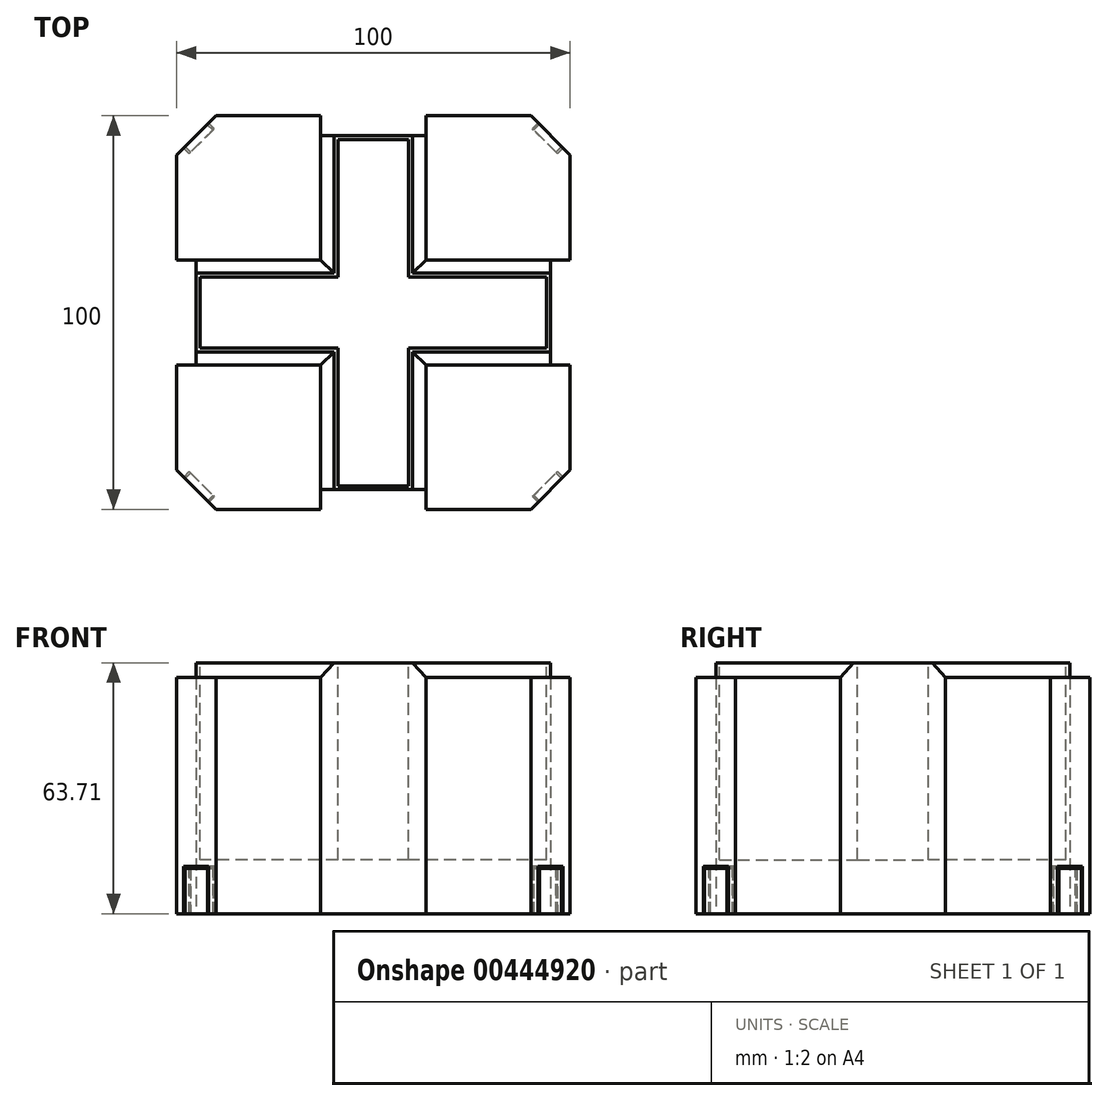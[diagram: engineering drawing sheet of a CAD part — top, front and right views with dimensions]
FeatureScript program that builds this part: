
annotation { "Feature Type Name" : "Feature", "Feature Type Description" : "" }
export const myFeature = defineFeature(function(context is Context, id is Id, definition is map)
    precondition{}
    {
        {
            var Q0;
            Q0=qCreatedBy(makeId("Front.planeOp"),FACE);
            var sketch = newSketch(context, id + "F0", { "sketchPlane" : qUnion([Q0])});
            skLineSegment(sketch, "E0.bottom", {"start": v(50, -30) * mm, "end": v(-50, -30) * mm});
            skLineSegment(sketch, "E0.left", {"start": v(50, -30) * mm, "end": v(50, 30) * mm});
            skLineSegment(sketch, "E0.right", {"start": v(-50, -30) * mm, "end": v(-50, 30) * mm});
            skPoint(sketch, "E0.middle", {"position": v(0, 0) * mm});
            skPoint(sketch, "E1.endSnap0", {"position": v(0, -30) * mm});
            skLineSegment(sketch, "E2", {"start": v(50, 30) * mm, "end": v(13.35, 30) * mm});
            skLineSegment(sketch, "E3", {"start": v(13.35, 30) * mm, "end": v(10, 33.7) * mm});
            skLineSegment(sketch, "E4", {"start": v(10, 33.7) * mm, "end": v(0, 33.7) * mm});
            skLineSegment(sketch, "E5.MirrorCS", {"start": v(-10, 33.7) * mm, "end": v(0, 33.7) * mm});
            skLineSegment(sketch, "E6.MirrorCS", {"start": v(-13.35, 30) * mm, "end": v(-10, 33.7) * mm});
            skLineSegment(sketch, "E7.MirrorCS", {"start": v(-50, 30) * mm, "end": v(-13.35, 30) * mm});
            skSolve(sketch);
        }
        {
            var Q0;
            Q0 = qSketchRegion(id + "F0", true);
            extrude(context, id + "F1", {"entities" : qUnion([Q0]), "endBound" : BoundingType.SYMMETRIC, "depth" : 100 * mm});
        }
        {
            var Q0;
            Q0=qCreatedBy(makeId("Right.planeOp"),FACE);
            var sketch = newSketch(context, id + "F2", { "sketchPlane" : qUnion([Q0])});
            skLineSegment(sketch, "E8", {"start": v(0, 33.7) * mm, "end": v(-10, 33.7) * mm});
            skLineSegment(sketch, "E9", {"start": v(-10, 33.7) * mm, "end": v(-13.35, 30) * mm});
            skLineSegment(sketch, "E10", {"start": v(-13.35, 30) * mm, "end": v(-50, 30) * mm});
            skLineSegment(sketch, "E11", {"start": v(-50, 30) * mm, "end": v(-50, -30) * mm});
            skLineSegment(sketch, "E12", {"start": v(-50, -30) * mm, "end": v(0, -30) * mm});
            skLineSegment(sketch, "E13.MirrorCS", {"start": v(0, 33.7) * mm, "end": v(10, 33.7) * mm});
            skLineSegment(sketch, "E14.MirrorCS", {"start": v(13.35, 30) * mm, "end": v(50, 30) * mm});
            skLineSegment(sketch, "E15.MirrorCS", {"start": v(50, 30) * mm, "end": v(50, -30) * mm});
            skLineSegment(sketch, "E16.MirrorCS", {"start": v(50, -30) * mm, "end": v(0, -30) * mm});
            skLineSegment(sketch, "E17.MirrorCS", {"start": v(10, 33.7) * mm, "end": v(13.35, 30) * mm});
            skSolve(sketch);
        }
        {
            var Q0;
            Q0 = qSketchRegion(id + "F2", true);
            extrude(context, id + "F3", {"entities" : qUnion([Q0]), "operationType" : NewBodyOperationType.ADD, "endBound" : BoundingType.SYMMETRIC, "depth" : 100 * mm});
        }
        {
            var Q0;
            Q0=makeQuery(id+"F3.boolean.opBoolean","MERGE",FACE,{"derivedFrom":[makeQuery(id+"F1.opExtrude","SWEPT_FACE",FACE,{"disambiguationData":[OSD([sQuery(id+"F0.wireOp",EDGE,"E0.right")])]}),makeQuery(id+"F3.opExtrude","CAP_FACE",FACE,{"disambiguationData":[OSD([sQuery(id+"F2.wireOp",EDGE,"E8"),sQuery(id+"F2.wireOp",EDGE,"E9"),sQuery(id+"F2.wireOp",EDGE,"E10"),sQuery(id+"F2.wireOp",EDGE,"E11"),sQuery(id+"F2.wireOp",EDGE,"E12"),sQuery(id+"F2.wireOp",EDGE,"E13.MirrorCS"),sQuery(id+"F2.wireOp",EDGE,"E14.MirrorCS"),sQuery(id+"F2.wireOp",EDGE,"E15.MirrorCS"),sQuery(id+"F2.wireOp",EDGE,"E16.MirrorCS"),sQuery(id+"F2.wireOp",EDGE,"E17.MirrorCS")])],"isStart":true})]});
            var sketch = newSketch(context, id + "F4", { "sketchPlane" : qUnion([Q0])});
            skLineSegment(sketch, "E18", {"start": v(-10, 33.7) * mm, "end": v(-13.35, 30) * mm});
            skLineSegment(sketch, "E19", {"start": v(-13.35, 30) * mm, "end": v(-13.35, -30) * mm});
            skLineSegment(sketch, "E20", {"start": v(-10, 33.7) * mm, "end": v(10, 33.7) * mm});
            skLineSegment(sketch, "E21", {"start": v(10, 33.7) * mm, "end": v(13.35, 30) * mm});
            skLineSegment(sketch, "E22", {"start": v(13.35, 30) * mm, "end": v(13.35, -30) * mm});
            skLineSegment(sketch, "E23", {"start": v(13.35, -30) * mm, "end": v(-13.35, -30) * mm});
            skSolve(sketch);
        }
        {
            var Q0;
            Q0 = qSketchRegion(id + "F4", true);
            extrude(context, id + "F5", {"entities" : qUnion([Q0]), "operationType" : NewBodyOperationType.REMOVE, "oppositeDirection" : true, "depth" : 5 * mm});
        }
        {
            var Q0;
            Q0=makeQuery(id+"F1.opExtrude","CAP_FACE",FACE,{"disambiguationData":[OSD([sQuery(id+"F0.wireOp",EDGE,"E0.bottom"),sQuery(id+"F0.wireOp",EDGE,"E0.left"),sQuery(id+"F0.wireOp",EDGE,"E0.right"),sQuery(id+"F0.wireOp",EDGE,"E2"),sQuery(id+"F0.wireOp",EDGE,"E3"),sQuery(id+"F0.wireOp",EDGE,"E4"),sQuery(id+"F0.wireOp",EDGE,"E5.MirrorCS"),sQuery(id+"F0.wireOp",EDGE,"E6.MirrorCS"),sQuery(id+"F0.wireOp",EDGE,"E7.MirrorCS")])],"isStart":false});
            var sketch = newSketch(context, id + "F6", { "sketchPlane" : qUnion([Q0])});
            skLineSegment(sketch, "E24", {"start": v(-13.35, 30) * mm, "end": v(-10, 33.7) * mm});
            skLineSegment(sketch, "E25", {"start": v(-10, 33.7) * mm, "end": v(10, 33.7) * mm});
            skLineSegment(sketch, "E26", {"start": v(10, 33.7) * mm, "end": v(13.35, 30) * mm});
            skLineSegment(sketch, "E27", {"start": v(13.35, 30) * mm, "end": v(13.35, -30) * mm});
            skLineSegment(sketch, "E28", {"start": v(13.35, -30) * mm, "end": v(-13.35, -30) * mm});
            skLineSegment(sketch, "E29", {"start": v(-13.35, -30) * mm, "end": v(-13.35, 30) * mm});
            skSolve(sketch);
        }
        {
            var Q0;
            Q0 = qSketchRegion(id + "F6", true);
            extrude(context, id + "F7", {"entities" : qUnion([Q0]), "operationType" : NewBodyOperationType.REMOVE, "oppositeDirection" : true, "depth" : 5 * mm});
        }
        {
            var Q0;
            Q0=makeQuery(id+"F3.boolean.opBoolean","MERGE",FACE,{"derivedFrom":[makeQuery(id+"F1.opExtrude","SWEPT_FACE",FACE,{"disambiguationData":[OSD([sQuery(id+"F0.wireOp",EDGE,"E0.left")])]}),makeQuery(id+"F3.opExtrude","CAP_FACE",FACE,{"disambiguationData":[OSD([sQuery(id+"F2.wireOp",EDGE,"E8"),sQuery(id+"F2.wireOp",EDGE,"E9"),sQuery(id+"F2.wireOp",EDGE,"E10"),sQuery(id+"F2.wireOp",EDGE,"E11"),sQuery(id+"F2.wireOp",EDGE,"E12"),sQuery(id+"F2.wireOp",EDGE,"E13.MirrorCS"),sQuery(id+"F2.wireOp",EDGE,"E14.MirrorCS"),sQuery(id+"F2.wireOp",EDGE,"E15.MirrorCS"),sQuery(id+"F2.wireOp",EDGE,"E16.MirrorCS"),sQuery(id+"F2.wireOp",EDGE,"E17.MirrorCS")])],"isStart":false})]});
            var sketch = newSketch(context, id + "F8", { "sketchPlane" : qUnion([Q0])});
            skLineSegment(sketch, "E30", {"start": v(-13.35, 30) * mm, "end": v(-10, 33.7) * mm});
            skLineSegment(sketch, "E31", {"start": v(-10, 33.7) * mm, "end": v(10, 33.7) * mm});
            skLineSegment(sketch, "E32", {"start": v(10, 33.7) * mm, "end": v(13.35, 30) * mm});
            skLineSegment(sketch, "E33", {"start": v(13.35, 30) * mm, "end": v(13.35, -30) * mm});
            skLineSegment(sketch, "E34", {"start": v(13.35, -30) * mm, "end": v(-13.35, -30) * mm});
            skLineSegment(sketch, "E35", {"start": v(-13.35, -30) * mm, "end": v(-13.35, 30) * mm});
            skSolve(sketch);
        }
        {
            var Q0;
            Q0 = qSketchRegion(id + "F8", true);
            extrude(context, id + "F9", {"entities" : qUnion([Q0]), "operationType" : NewBodyOperationType.REMOVE, "oppositeDirection" : true, "depth" : 5 * mm});
        }
        {
            var Q0;
            Q0=makeQuery(id+"F1.opExtrude","CAP_FACE",FACE,{"disambiguationData":[OSD([sQuery(id+"F0.wireOp",EDGE,"E0.bottom"),sQuery(id+"F0.wireOp",EDGE,"E0.left"),sQuery(id+"F0.wireOp",EDGE,"E0.right"),sQuery(id+"F0.wireOp",EDGE,"E2"),sQuery(id+"F0.wireOp",EDGE,"E3"),sQuery(id+"F0.wireOp",EDGE,"E4"),sQuery(id+"F0.wireOp",EDGE,"E5.MirrorCS"),sQuery(id+"F0.wireOp",EDGE,"E6.MirrorCS"),sQuery(id+"F0.wireOp",EDGE,"E7.MirrorCS")])],"isStart":true});
            var sketch = newSketch(context, id + "F10", { "sketchPlane" : qUnion([Q0])});
            skLineSegment(sketch, "E36", {"start": v(-13.35, 30) * mm, "end": v(-10, 33.7) * mm});
            skLineSegment(sketch, "E37", {"start": v(-10, 33.7) * mm, "end": v(10, 33.7) * mm});
            skLineSegment(sketch, "E38", {"start": v(10, 33.7) * mm, "end": v(13.35, 30) * mm});
            skLineSegment(sketch, "E39", {"start": v(13.35, 30) * mm, "end": v(13.35, -30) * mm});
            skLineSegment(sketch, "E40", {"start": v(13.35, -30) * mm, "end": v(-13.35, -30) * mm});
            skLineSegment(sketch, "E41", {"start": v(-13.35, -30) * mm, "end": v(-13.35, 30) * mm});
            skSolve(sketch);
        }
        {
            var Q0;
            Q0 = qSketchRegion(id + "F10", true);
            extrude(context, id + "F11", {"entities" : qUnion([Q0]), "operationType" : NewBodyOperationType.REMOVE, "oppositeDirection" : true, "depth" : 5 * mm});
        }
        {
            var Q0;
            Q0=makeQuery(id+"F1.opExtrude","CAP_EDGE",EDGE,{"disambiguationData":[OSD([sQuery(id+"F0.wireOp",EDGE,"E0.left")])],"isStart":false});
            var Q1;
            Q1=makeQuery(id+"F1.opExtrude","CAP_EDGE",EDGE,{"disambiguationData":[OSD([sQuery(id+"F0.wireOp",EDGE,"E0.left")])],"isStart":true});
            var Q2;
            Q2=makeQuery(id+"F1.opExtrude","CAP_EDGE",EDGE,{"disambiguationData":[OSD([sQuery(id+"F0.wireOp",EDGE,"E0.right")])],"isStart":true});
            var Q3;
            Q3=makeQuery(id+"F1.opExtrude","CAP_EDGE",EDGE,{"disambiguationData":[OSD([sQuery(id+"F0.wireOp",EDGE,"E0.right")])],"isStart":false});
            chamfer(context, id + "F12", {"entities" : qUnion([Q0, Q1, Q2, Q3]), "width" : 10 * mm, "tangentPropagation" : true});
        }
        {
            var Q0;
            {var subQ0=sQuery(id+"F0.wireOp",EDGE,"E0.right");Q0=makeQuery(id+"F12.opChamfer","BLEND_FACE",FACE,{"disambiguationData":[OSD([subQ0]),TDD([makeQuery(id+"F1.opExtrude","CAP_EDGE",EDGE,{"disambiguationData":[OSD([subQ0])],"isStart":true})])]});}
            var sketch = newSketch(context, id + "F13", { "sketchPlane" : qUnion([Q0])});
            skLineSegment(sketch, "E42", {"start": v(-4.48, -30) * mm, "end": v(-4.48, -18) * mm});
            skLineSegment(sketch, "E43", {"start": v(-4.48, -18) * mm, "end": v(4.52, -18) * mm});
            skLineSegment(sketch, "E44", {"start": v(4.52, -18) * mm, "end": v(4.52, -30) * mm});
            skSolve(sketch);
        }
        {
            var Q0;
            {var subQ0=sQuery(id+"F13.wireOp",EDGE,"E42");Q0=makeQuery(id+"F13.imprint","IMPRINT",FACE,{"disambiguationData":[TD([[makeQuery(id+"F13.imprint","IMPRINT",EDGE,{"derivedFrom":subQ0}),-1.0]])]});}
            extrude(context, id + "F14", {"entities" : qUnion([Q0]), "operationType" : NewBodyOperationType.REMOVE, "oppositeDirection" : true, "depth" : 2 * mm});
        }
        {
            var Q0;
            Q0=makeQuery(id+"F14.boolean.opBoolean","COPY",FACE,{"derivedFrom":makeQuery(id+"F14.opExtrude","CAP_FACE",FACE,{"disambiguationData":[OSD([sQuery(id+"F0.wireOp",EDGE,"E0.bottom"),sQuery(id+"F0.wireOp",EDGE,"E0.right"),sQuery(id+"F13.wireOp",EDGE,"E42"),sQuery(id+"F13.wireOp",EDGE,"E43"),sQuery(id+"F13.wireOp",EDGE,"E44")])],"isStart":false})});
            var sketch = newSketch(context, id + "F15", { "sketchPlane" : qUnion([Q0])});
            skLineSegment(sketch, "E45", {"start": v(-3.98, -30) * mm, "end": v(-3.98, -18.5) * mm});
            skLineSegment(sketch, "E46", {"start": v(-3.98, -18.5) * mm, "end": v(4.02, -18.5) * mm});
            skLineSegment(sketch, "E47", {"start": v(4.02, -18.5) * mm, "end": v(4.02, -30) * mm});
            skLineSegment(sketch, "E48", {"start": v(4.02, -30) * mm, "end": v(-3.98, -30) * mm});
            skSolve(sketch);
        }
        {
            var Q0;
            Q0=makeQuery(id+"F15.imprint","IMPRINT",FACE,{"disambiguationData":[TD([[makeQuery(id+"F15.imprint","IMPRINT",EDGE,{"derivedFrom":sQuery(id+"F15.wireOp",EDGE,"E45")}),-1.0]])]});
            extrude(context, id + "F16", {"entities" : qUnion([Q0]), "operationType" : NewBodyOperationType.ADD, "depth" : 2 * mm});
        }
        {
            var Q0;
            {var subQ0=sQuery(id+"F0.wireOp",EDGE,"E0.right");Q0=makeQuery(id+"F12.opChamfer","BLEND_FACE",FACE,{"disambiguationData":[OSD([subQ0]),TDD([makeQuery(id+"F1.opExtrude","CAP_EDGE",EDGE,{"disambiguationData":[OSD([subQ0])],"isStart":false})])]});}
            var sketch = newSketch(context, id + "F17", { "sketchPlane" : qUnion([Q0])});
            skLineSegment(sketch, "E49", {"start": v(-4.48, -30) * mm, "end": v(-4.48, -18) * mm});
            skLineSegment(sketch, "E50", {"start": v(-4.48, -18) * mm, "end": v(4.52, -18) * mm});
            skLineSegment(sketch, "E51", {"start": v(4.52, -18) * mm, "end": v(4.52, -30) * mm});
            skSolve(sketch);
        }
        {
            var Q0;
            {var subQ0=sQuery(id+"F17.wireOp",EDGE,"E49");Q0=makeQuery(id+"F17.imprint","IMPRINT",FACE,{"disambiguationData":[TD([[makeQuery(id+"F17.imprint","IMPRINT",EDGE,{"derivedFrom":subQ0}),-1.0]])]});}
            extrude(context, id + "F18", {"entities" : qUnion([Q0]), "operationType" : NewBodyOperationType.REMOVE, "oppositeDirection" : true, "depth" : 2 * mm});
        }
        {
            var Q0;
            Q0=makeQuery(id+"F18.boolean.opBoolean","COPY",FACE,{"derivedFrom":makeQuery(id+"F18.opExtrude","CAP_FACE",FACE,{"disambiguationData":[OSD([sQuery(id+"F0.wireOp",EDGE,"E0.bottom"),sQuery(id+"F0.wireOp",EDGE,"E0.right"),sQuery(id+"F17.wireOp",EDGE,"E49"),sQuery(id+"F17.wireOp",EDGE,"E50"),sQuery(id+"F17.wireOp",EDGE,"E51")])],"isStart":false})});
            var sketch = newSketch(context, id + "F19", { "sketchPlane" : qUnion([Q0])});
            skLineSegment(sketch, "E52", {"start": v(-3.98, -30) * mm, "end": v(-3.98, -18.5) * mm});
            skLineSegment(sketch, "E53", {"start": v(-3.98, -18.5) * mm, "end": v(4.02, -18.5) * mm});
            skLineSegment(sketch, "E54", {"start": v(4.02, -18.5) * mm, "end": v(4.02, -30) * mm});
            skLineSegment(sketch, "E55", {"start": v(4.02, -30) * mm, "end": v(-3.98, -30) * mm});
            skSolve(sketch);
        }
        {
            var Q0;
            {var subQ0=sQuery(id+"F0.wireOp",EDGE,"E0.left");Q0=makeQuery(id+"F12.opChamfer","BLEND_FACE",FACE,{"disambiguationData":[OSD([subQ0]),TDD([makeQuery(id+"F1.opExtrude","CAP_EDGE",EDGE,{"disambiguationData":[OSD([subQ0])],"isStart":false})])]});}
            var sketch = newSketch(context, id + "F20", { "sketchPlane" : qUnion([Q0])});
            skLineSegment(sketch, "E56", {"start": v(-4.48, -30) * mm, "end": v(-4.48, -18) * mm});
            skLineSegment(sketch, "E57", {"start": v(-4.48, -18) * mm, "end": v(4.52, -18) * mm});
            skLineSegment(sketch, "E58", {"start": v(4.52, -18) * mm, "end": v(4.52, -30) * mm});
            skLineSegment(sketch, "E59", {"start": v(4.52, -30) * mm, "end": v(-4.48, -30) * mm});
            skSolve(sketch);
        }
        {
            var Q0;
            Q0=makeQuery(id+"F20.imprint","IMPRINT",FACE,{"disambiguationData":[TD([[makeQuery(id+"F20.imprint","IMPRINT",EDGE,{"derivedFrom":sQuery(id+"F20.wireOp",EDGE,"E56")}),-1.0]])]});
            extrude(context, id + "F21", {"entities" : qUnion([Q0]), "operationType" : NewBodyOperationType.REMOVE, "oppositeDirection" : true, "depth" : 2 * mm});
        }
        {
            var Q0;
            Q0=makeQuery(id+"F21.boolean.opBoolean","COPY",FACE,{"derivedFrom":makeQuery(id+"F21.opExtrude","CAP_FACE",FACE,{"disambiguationData":[OSD([sQuery(id+"F20.wireOp",EDGE,"E56"),sQuery(id+"F20.wireOp",EDGE,"E57"),sQuery(id+"F20.wireOp",EDGE,"E58"),sQuery(id+"F20.wireOp",EDGE,"E59")])],"isStart":false})});
            var sketch = newSketch(context, id + "F22", { "sketchPlane" : qUnion([Q0])});
            skLineSegment(sketch, "E60", {"start": v(-3.98, -30) * mm, "end": v(-3.98, -18.5) * mm});
            skLineSegment(sketch, "E61", {"start": v(-3.98, -18.5) * mm, "end": v(4.02, -18.5) * mm});
            skLineSegment(sketch, "E62", {"start": v(4.02, -18.5) * mm, "end": v(4.02, -30) * mm});
            skLineSegment(sketch, "E63", {"start": v(4.02, -30) * mm, "end": v(-3.98, -30) * mm});
            skSolve(sketch);
        }
        {
            var Q0;
            Q0 = qSketchRegion(id + "F22", true);
            extrude(context, id + "F23", {"entities" : qUnion([Q0]), "operationType" : NewBodyOperationType.ADD, "depth" : 2 * mm});
        }
        {
            var Q0;
            {var subQ0=sQuery(id+"F0.wireOp",EDGE,"E0.left");Q0=makeQuery(id+"F12.opChamfer","BLEND_FACE",FACE,{"disambiguationData":[OSD([subQ0]),TDD([makeQuery(id+"F1.opExtrude","CAP_EDGE",EDGE,{"disambiguationData":[OSD([subQ0])],"isStart":true})])]});}
            var sketch = newSketch(context, id + "F24", { "sketchPlane" : qUnion([Q0])});
            skLineSegment(sketch, "E64", {"start": v(-4.48, -30) * mm, "end": v(-4.48, -18) * mm});
            skLineSegment(sketch, "E65", {"start": v(-4.48, -18) * mm, "end": v(4.52, -18) * mm});
            skLineSegment(sketch, "E66", {"start": v(4.52, -18) * mm, "end": v(4.52, -30) * mm});
            skLineSegment(sketch, "E67", {"start": v(4.52, -30) * mm, "end": v(-4.48, -30) * mm});
            skSolve(sketch);
        }
        {
            var Q0;
            Q0 = qSketchRegion(id + "F24", true);
            extrude(context, id + "F25", {"entities" : qUnion([Q0]), "operationType" : NewBodyOperationType.REMOVE, "oppositeDirection" : true, "depth" : 2 * mm});
        }
        {
            var Q0;
            Q0=makeQuery(id+"F25.boolean.opBoolean","COPY",FACE,{"derivedFrom":makeQuery(id+"F25.opExtrude","CAP_FACE",FACE,{"disambiguationData":[OSD([sQuery(id+"F24.wireOp",EDGE,"E64"),sQuery(id+"F24.wireOp",EDGE,"E65"),sQuery(id+"F24.wireOp",EDGE,"E66"),sQuery(id+"F24.wireOp",EDGE,"E67")])],"isStart":false})});
            var sketch = newSketch(context, id + "F26", { "sketchPlane" : qUnion([Q0])});
            skLineSegment(sketch, "E68", {"start": v(-3.98, -30) * mm, "end": v(-3.98, -18.5) * mm});
            skLineSegment(sketch, "E69", {"start": v(-3.98, -18.5) * mm, "end": v(4.02, -18.5) * mm});
            skLineSegment(sketch, "E70", {"start": v(4.02, -18.5) * mm, "end": v(4.02, -30) * mm});
            skLineSegment(sketch, "E71", {"start": v(4.02, -30) * mm, "end": v(-3.98, -30) * mm});
            skSolve(sketch);
        }
        {
            var Q0;
            Q0 = qSketchRegion(id + "F26", true);
            extrude(context, id + "F27", {"entities" : qUnion([Q0]), "operationType" : NewBodyOperationType.ADD, "depth" : 2 * mm});
        }
        {
            var Q0;
            Q0=makeQuery(id+"F19.imprint","IMPRINT",FACE,{"disambiguationData":[TD([[makeQuery(id+"F19.imprint","IMPRINT",EDGE,{"derivedFrom":sQuery(id+"F19.wireOp",EDGE,"E52")}),-1.0]])]});
            extrude(context, id + "F28", {"entities" : qUnion([Q0]), "operationType" : NewBodyOperationType.ADD, "depth" : 2 * mm});
        }
        {
            var Q0;
            Q0=makeQuery(id+"F3.boolean.opBoolean","MERGE",FACE,{"derivedFrom":[makeQuery(id+"F1.opExtrude","SWEPT_FACE",FACE,{"disambiguationData":[OSD([sQuery(id+"F0.wireOp",EDGE,"E4"),sQuery(id+"F0.wireOp",EDGE,"E5.MirrorCS")])]}),makeQuery(id+"F3.opExtrude","SWEPT_FACE",FACE,{"disambiguationData":[OSD([sQuery(id+"F2.wireOp",EDGE,"E8"),sQuery(id+"F2.wireOp",EDGE,"E13.MirrorCS")])]})]});
            var sketch = newSketch(context, id + "F29", { "sketchPlane" : qUnion([Q0])});
            skLineSegment(sketch, "E72", {"start": v(-44, -9) * mm, "end": v(-44, 9) * mm});
            skLineSegment(sketch, "E73", {"start": v(-44, 9) * mm, "end": v(-9, 9) * mm});
            skLineSegment(sketch, "E74", {"start": v(-9, 9) * mm, "end": v(-9, 44) * mm});
            skLineSegment(sketch, "E75", {"start": v(-9, 44) * mm, "end": v(9, 44) * mm});
            skLineSegment(sketch, "E76", {"start": v(9, 44) * mm, "end": v(9, 9) * mm});
            skLineSegment(sketch, "E77", {"start": v(9, 9) * mm, "end": v(44, 9) * mm});
            skLineSegment(sketch, "E78", {"start": v(44, 9) * mm, "end": v(44, -9) * mm});
            skLineSegment(sketch, "E79", {"start": v(44, -9) * mm, "end": v(9, -9) * mm});
            skLineSegment(sketch, "E80", {"start": v(9, -9) * mm, "end": v(9, -44) * mm});
            skLineSegment(sketch, "E81", {"start": v(9, -44) * mm, "end": v(-9, -44) * mm});
            skLineSegment(sketch, "E82", {"start": v(-9, -44) * mm, "end": v(-9, -9) * mm});
            skLineSegment(sketch, "E83", {"start": v(-9, -9) * mm, "end": v(-44, -9) * mm});
            skSolve(sketch);
        }
        {
            var Q0;
            Q0=makeQuery(id+"F29.imprint","IMPRINT",FACE,{"disambiguationData":[TD([[makeQuery(id+"F29.imprint","IMPRINT",EDGE,{"derivedFrom":sQuery(id+"F29.wireOp",EDGE,"E72")}),-1.0]])]});
            extrude(context, id + "F30", {"entities" : qUnion([Q0]), "operationType" : NewBodyOperationType.REMOVE, "oppositeDirection" : true, "depth" : 50 * mm});
        }
    });
